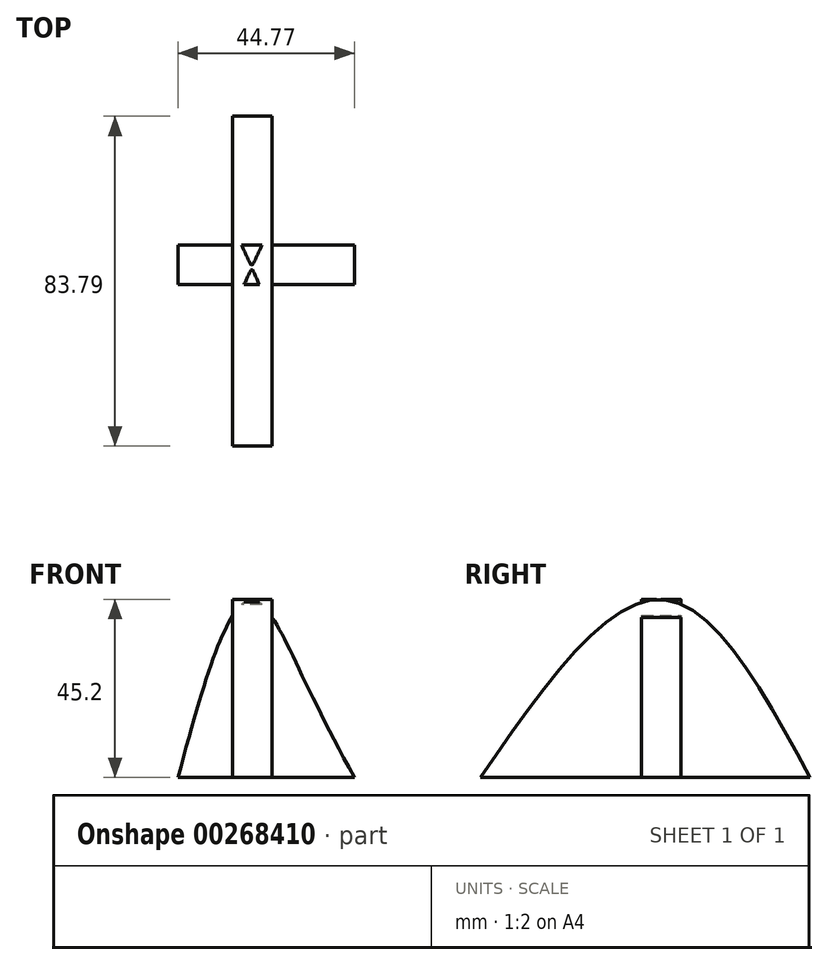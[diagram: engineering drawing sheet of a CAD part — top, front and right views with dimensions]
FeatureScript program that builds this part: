
annotation { "Feature Type Name" : "Feature", "Feature Type Description" : "" }
export const myFeature = defineFeature(function(context is Context, id is Id, definition is map)
    precondition{}
    {
        {
            var Q0;
            Q0=qCreatedBy(makeId("Right.planeOp"),FACE);
            var sketch = newSketch(context, id + "F0", { "sketchPlane" : qUnion([Q0])});
            skFitSpline(sketch, "E0", {"points": [v(-46, 0) * mm, v(0, 45.18) * mm, v(37.79, 0) * mm], "startDerivative": vector(93.2, 134.59) * mm, "endDerivative": vector(74.23, -136.63) * mm});
            skLineSegment(sketch, "E1", {"start": v(-46, 0) * mm, "end": v(37.79, 0) * mm});
            skSolve(sketch);
        }
        {
            var Q0;
            Q0=qCreatedBy(makeId("Front.planeOp"),FACE);
            var sketch = newSketch(context, id + "F1", { "sketchPlane" : qUnion([Q0])});
            skFitSpline(sketch, "E2", {"points": [v(-18.9, 0) * mm, v(0, 45.18) * mm, v(25.88, 0) * mm], "startDerivative": vector(46.85, 179.6) * mm, "endDerivative": vector(89.06, -159.55) * mm});
            skLineSegment(sketch, "E3", {"start": v(-18.9, 0) * mm, "end": v(25.88, 0) * mm});
            skSolve(sketch);
        }
        {
            var Q0;
            Q0 = qSketchRegion(id + "F0", true);
            extrude(context, id + "F2", {"entities" : qUnion([Q0]), "depth" : 5 * mm, "hasSecondDirection" : true, "secondDirectionOppositeDirection" : true, "secondDirectionDepth" : 5 * mm});
        }
        {
            var Q0;
            Q0 = qSketchRegion(id + "F1", true);
            extrude(context, id + "F3", {"entities" : qUnion([Q0]), "operationType" : NewBodyOperationType.ADD, "depth" : 5 * mm, "hasSecondDirection" : true, "secondDirectionOppositeDirection" : true, "secondDirectionDepth" : 5 * mm});
        }
    });
